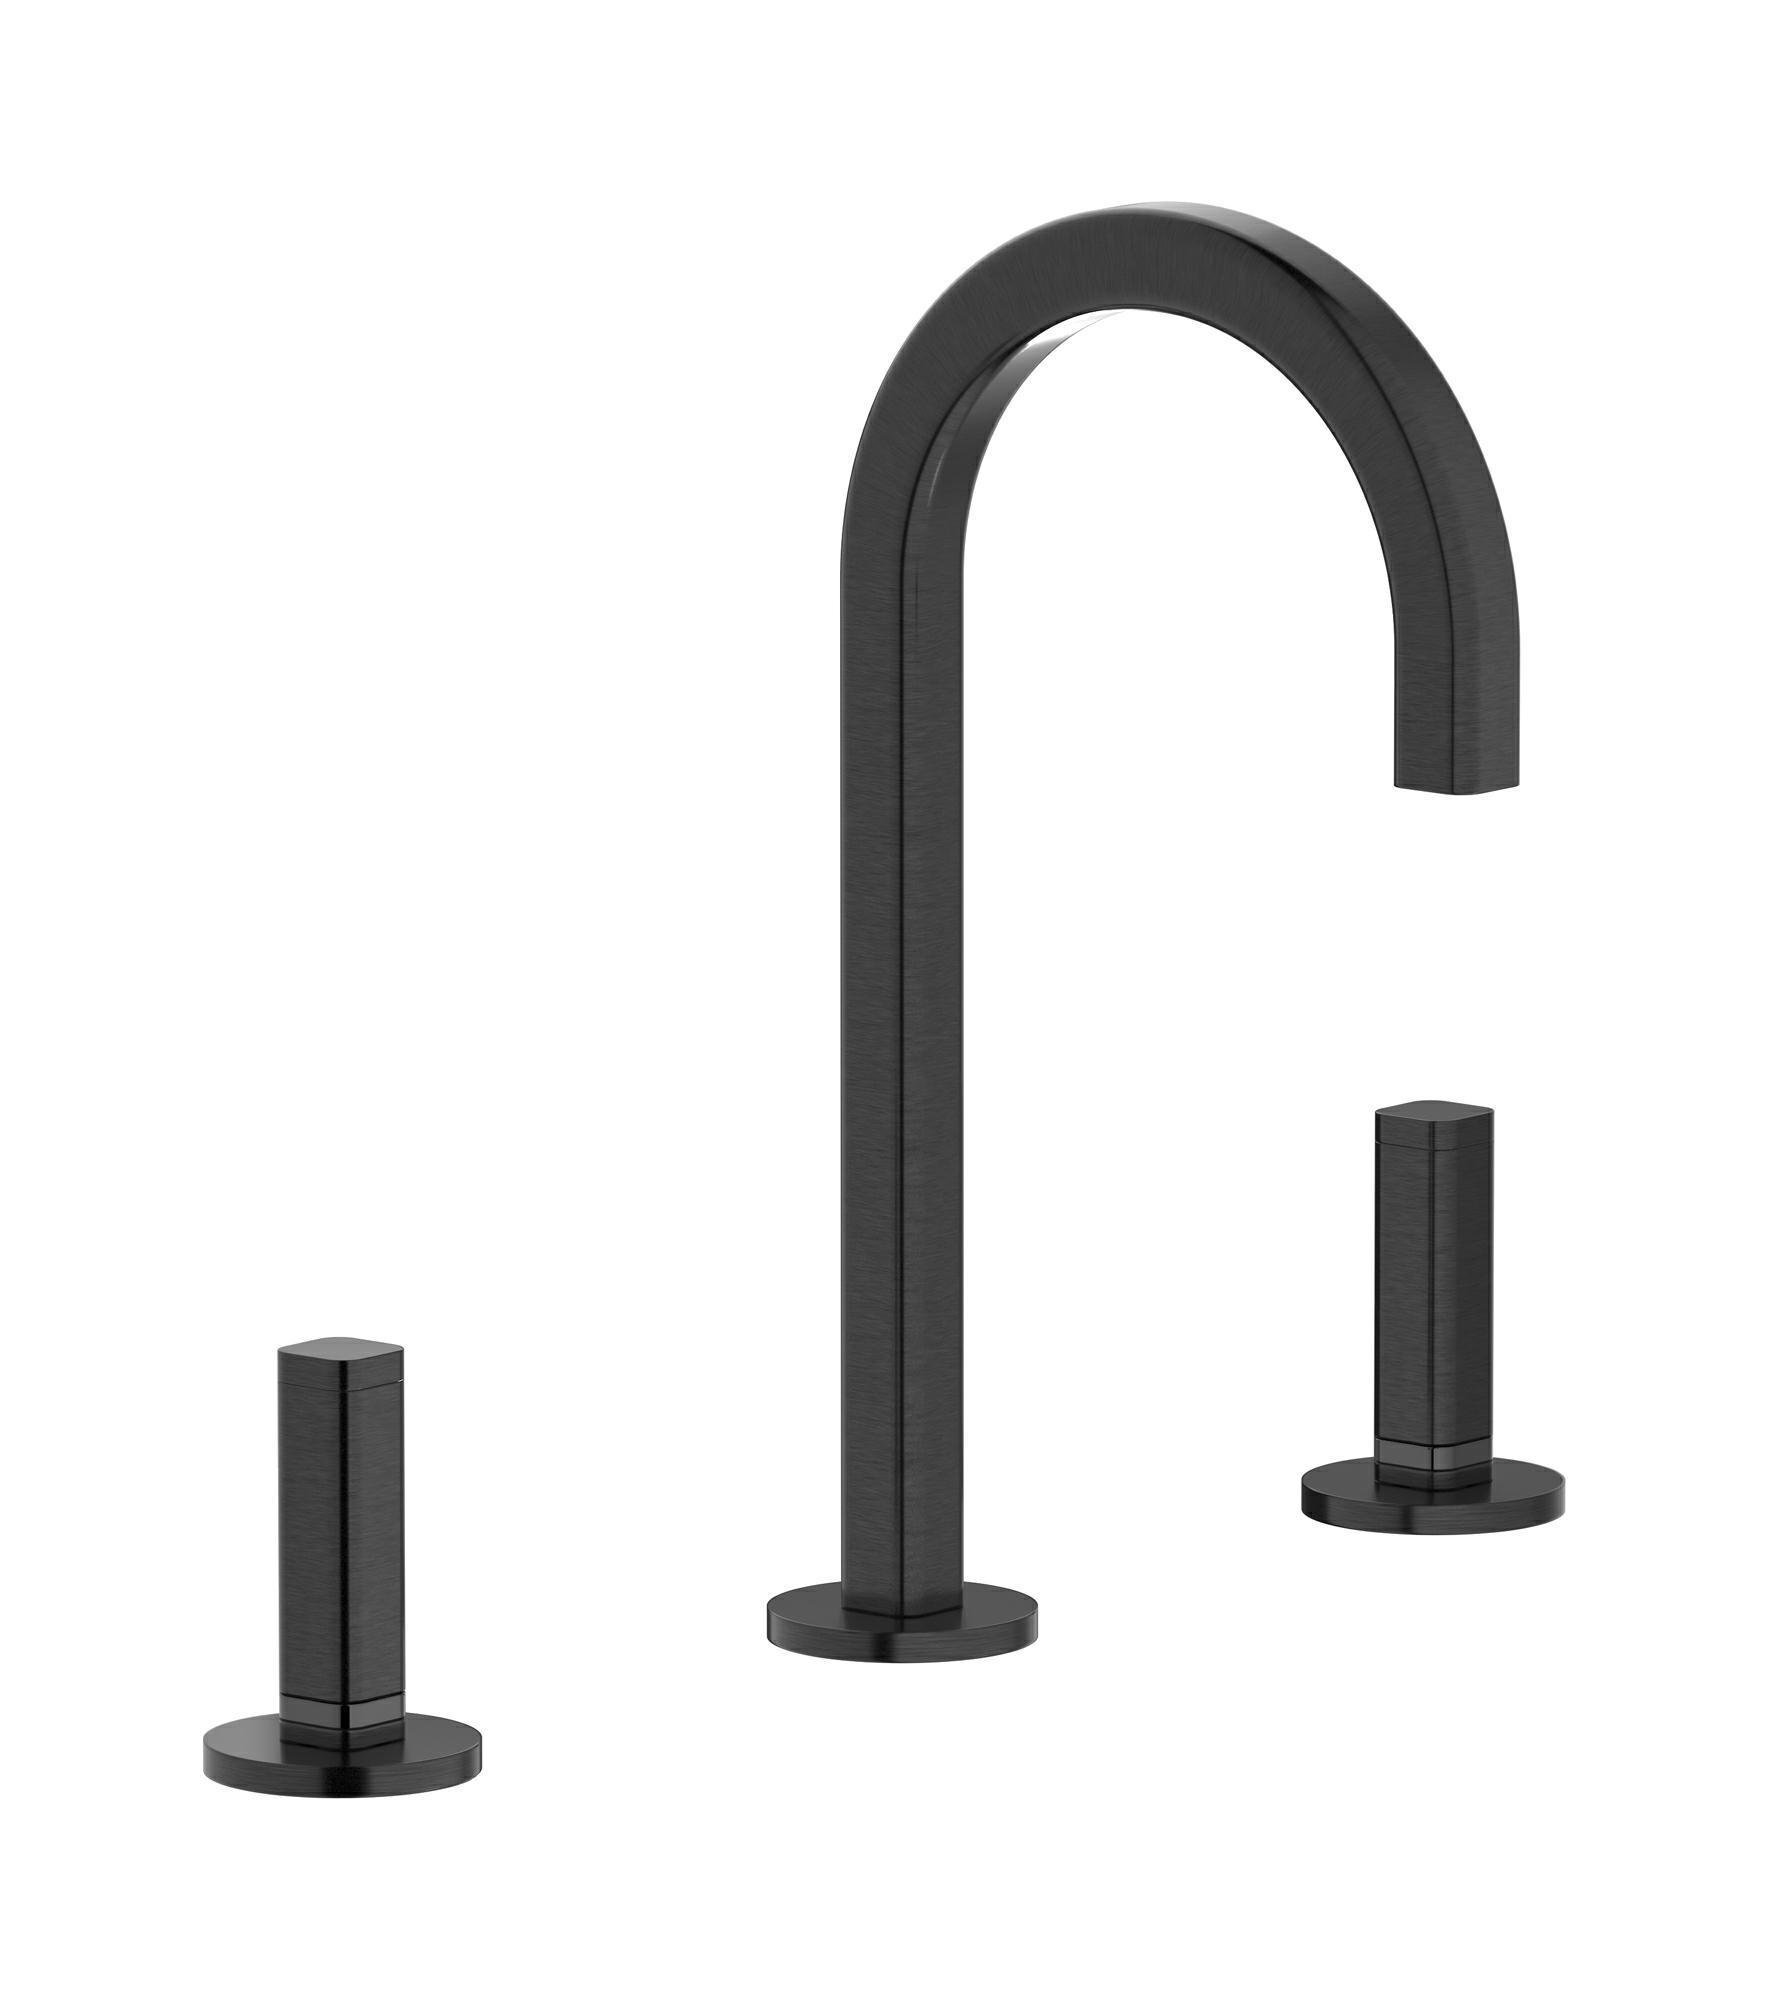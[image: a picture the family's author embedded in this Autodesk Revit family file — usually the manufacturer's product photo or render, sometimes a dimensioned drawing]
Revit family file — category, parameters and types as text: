
# Revit family: EI392_3
name_source: partatom
category: Apparecchi idraulici
units: mm (PartAtom-declared; Revit-internal decimal feet)

## family parameters
Basato su piano di lavoro = No
Condiviso = No
Mantieni orientamento annotazione = No
Numero OmniClass = 23.45.55.17
Punto di calcolo locali = No
Quota connettore circolare = Usa diametro
Sempre verticale = Sì
Taglio con vuoti quando caricato = No
Tipo di parte = Normale
Titolo OmniClass = Mixing Faucets

## types (12) — shared parameters
Cold water inlet = 10 mm  [stored 0.0328084 ft]
Commenti sul tipo = Washbasin
Connessione CW = No
Connessione HW = No
Connessione di scarico = No
Connessione di ventilazione = No
Descrizione = Three hole washbasin complete
Hot water inlet = 10 mm  [stored 0.0328084 ft]
Produttore = IB Rubinetterie S.p.A.
URL = https://www.weareib.it
zero-valued in all types: Prospetto di default

## per-type parameters (varying)
| type | Finishes surface | Immagine tipo | Modello |
| Chrome | IB_Chrome | EI392CC_3.jpg | EI392CC_3 |
| Brushed nickel | IB_Brushed nickel | EI392SS_3.jpg | EI392SS_3 |
| Natural brass | IB_Brass | EI392ON_3.jpg | EI392ON_3 |
| Matt black | IB_matt black | EI392NP_3.jpg | EI392NP_3 |
| Black chrome | IB_Black chrome | EI392CF_3.jpg | EI392CF_3 |
| Brushed black chrome | IB_Brushed black chrome | EI392CS_3.jpg | EI392CS_3 |
| Pale gold | IB_Pale gold | EI392II_3.jpg | EI392II_3 |
| Brushed pale gold | IB_brushed pale gold | EI392IS_3.jpg | EI392IS_3 |
| Rose gold | IB_Rose gold | EI392RS_3.jpg | EI392RS_3 |
| Brushed rose gold | IB_Brushed rose gold | EI392SR_3.jpg | EI392SR_3 |
| Gold | IB_gold | EI392OO_3.jpg | EI392OO_3 |
| Brushed gold | IB_brushed gold | EI392OS_3.jpg | EI392OS_3 |

note: [stored X ft] marks values corroborated as IEEE doubles in the binary element streams (Revit-internal decimal feet)
